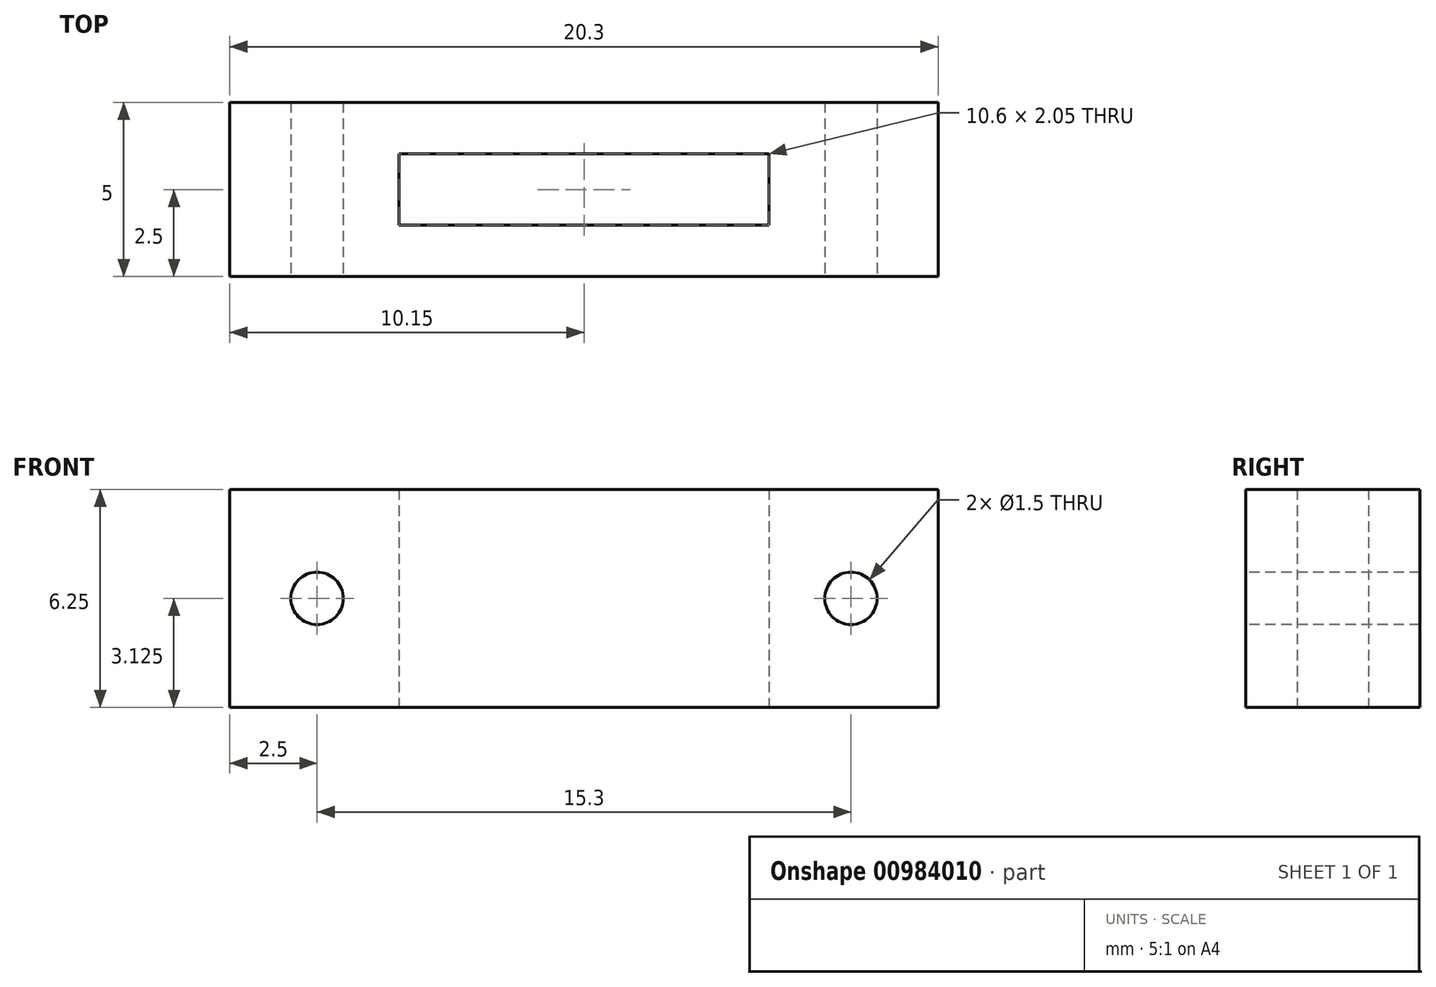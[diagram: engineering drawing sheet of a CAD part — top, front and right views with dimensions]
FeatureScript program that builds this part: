
annotation { "Feature Type Name" : "Feature", "Feature Type Description" : "" }
export const myFeature = defineFeature(function(context is Context, id is Id, definition is map)
    precondition{}
    {
        {
            var Q0;
            Q0=qCreatedBy(makeId("Top.planeOp"),FACE);
            var sketch = newSketch(context, id + "F0", { "sketchPlane" : qUnion([Q0])});
            skLineSegment(sketch, "E0.bottom", {"start": v(10.15, -2.5) * mm, "end": v(-10.15, -2.5) * mm});
            skLineSegment(sketch, "E0.top", {"start": v(10.15, 2.5) * mm, "end": v(-10.15, 2.5) * mm});
            skLineSegment(sketch, "E0.left", {"start": v(10.15, -2.5) * mm, "end": v(10.15, 2.5) * mm});
            skLineSegment(sketch, "E0.right", {"start": v(-10.15, -2.5) * mm, "end": v(-10.15, 2.5) * mm});
            skPoint(sketch, "E0.middle", {"position": v(0, 0) * mm});
            skLineSegment(sketch, "E1.bottom", {"start": v(-5.3, 1.02) * mm, "end": v(5.3, 1.02) * mm});
            skLineSegment(sketch, "E1.top", {"start": v(-5.3, -1.02) * mm, "end": v(5.3, -1.02) * mm});
            skLineSegment(sketch, "E1.left", {"start": v(-5.3, 1.02) * mm, "end": v(-5.3, -1.03) * mm});
            skLineSegment(sketch, "E1.right", {"start": v(5.3, 1.03) * mm, "end": v(5.3, -1.03) * mm});
            skSolve(sketch);
        }
        {
            var Q0;
            Q0=qSketchRegion(id+"F0",true);
            extrude(context, id + "F1", {"entities" : qUnion([Q0]), "depth" : 6.25 * mm, "offsetDistance" : 25 * mm});
        }
        {
            var Q0;
            Q0=qCreatedBy(makeId("Front.planeOp"),FACE);
            var sketch = newSketch(context, id + "F2", { "sketchPlane" : qUnion([Q0])});
            skCircle(sketch, "E2", {"center": v(-7.65, 3.12) * mm, "radius": 0.75 * mm});
            skCircle(sketch, "E3", {"center": v(7.65, 3.12) * mm, "radius": 0.75 * mm});
            skLineSegment(sketch, "E4", {"start": v(-7.65, 3.12) * mm, "end": v(7.65, 3.12) * mm, "construction": true});
            skSolve(sketch);
        }
        {
            var Q0;
            Q0=qSketchRegion(id+"F2",true);
            extrude(context, id + "F3", {"entities" : qUnion([Q0]), "operationType" : NewBodyOperationType.REMOVE, "endBound" : BoundingType.SYMMETRIC, "oppositeDirection" : true, "depth" : 7.8 * mm, "offsetDistance" : 25 * mm});
        }
    });
